# Revit family: ON5DRX-NRG
name_source: partatom
category: Mechanical Equipment
units: mm (PartAtom-declared; Revit-internal decimal feet)

## family parameters
Always vertical = Yes
Cut with Voids When Loaded = No
OmniClass Number = 23.40.40.11.17
OmniClass Title = Refrigerated Cases
Part Type = Normal
Room Calculation Point = No
Round Connector Dimension = Use Radius
Shared = No
Work Plane-Based = Yes

## types (8) — shared parameters
24" Shelf = Yes
BOTTOM ELECTRICAL = Yes
BOTTOM REFRIGERATION PIPING = Yes
Certifications = NSF 7, UL471, CSA
DATE = 03/21/2017
DRAIN PIPING = Yes
Default Elevation = 48"
Description = Rear Load Multi-Deck Merchandiser with Synerg-E™
Discharge Air Velocity (FPM) = 260 FPM
EQUIPMENT DESCRIPTION = Rear Load Multi-Deck Merchandiser with Synerg-E™
EQUIPMENT MARK = ON5DRX-NRG
GLASS = Glass
Height = 81 11/16"
High Efficiency Amps = 1 A
High Power (Cornice) Amps = 0 A
Item Description = Rear Load Multi-Deck Merchandiser with Synerg-E™
LF STD END = Yes
Legend Number = ON5DRX-NRG
Manufacturer = HILL PHOENIX
Model = ON5DRX-NRG
PAINTED METAL UPPER SHELF = PAINTED SHELVES
REAR REFRIGERATION PIPING = Yes
REFRIGERATION PIPING = COPPER PIPE
RT STD END = Yes
Refgn = 8 3/4"
STAINLESS STEEL = GALVANIZED STEEL
Standard Power Amps = 0 A
Superheat Set Point @ Bulb (°F) = 6 - 8 °F
TOP ELECTRICAL = Yes
TOP REFRIGERATION PIPING = Yes
Timed-Off Defrost Termination Temp = 42 °F
URL = http://www.hillphoenix.com
Width = 45 1/4"
zero-valued in all types: Defrosts Per Day, Number of Fans

## per-type parameters (varying)
| type | BTUH Conventional | BTUH Parallel | CENTER LINE | DRAIN LINE | Discharge Air (°F) | Door | Evaporator (°F) | High Efficiency Watts | High Power (Cornice) Watts | Length | Length of Cases | Light Length | Lights Per Row | Number of Doors | Standard Power Watts | Timed-Off Defrost Fail-Safe (Min) |
| 08' | 1478 | 1293 | 48" | 48" | 32 °F | Door_8 : 08'(Dairy,Deli,Cut Produce) | 28 °F | 50 W | 24 W | 96" | 96" | 3' | 2 | 2 | 9 W | 40 |
| 12' | 1435 | 1256 | 72" | 72" | 32 °F | Door_12 : 12'(Dairy,Deli,Cut Produce) | 28 °F | 100 W | 45 W | 144" | 144" | 4' | 3 | 3 | 18 W | 30 (Min) |
| Sample 1 (8') | 1404 | 1229 | 48" | 48" | 32 °F | Door_8 : 08'(Dairy,Deli,Cut Produce) | 28 °F | 50 W | 24 W | 96" | 96" | 3' | 2 | 2 | 9 W | 40 (Min) |
| Std. Dairy | 1380 | 1208 | 48" | 48" | 32 °F | Door_8 : 08'(Dairy,Deli,Cut Produce) | 28 °F | 67 W | 43 W | 96" | 96" | 4' | 2 | 2 | 24 W | 40 (Min) |
| 2.5" Ext | 1152 | 1120 | 48" | 48" | 37 °F | Door_8 : 08'(Dairy,Deli,Cut Produce) | 34 °F | 67 W | 43 W | 96" | 96" | 4' | 2 | 2 | 24 W | 40 (Min) |
| 5" Ext | 1101 | 1085 | 48" | 48" | 37 °F | Door_8 : 08'(Dairy,Deli,Cut Produce) | 34 °F | 67 W | 43 W | 96" | 96" | 4' | 2 | 2 | 24 W | 40 (Min) |
| 7.5" Ext | 1068 | 1053 | 48" | 48" | 37 °F | Door_8 : 08'(Dairy,Deli,Cut Produce) | 34 °F | 67 W | 43 W | 96" | 96" | 4' | 2 | 2 | 24 W | 40 (Min) |
| Sample 1 (6') 2 | 1404 | 1229 | 36" | 48" | 32 °F | Door_8 : 08'(Dairy,Deli,Cut Produce) | 28 °F | 50 W | 24 W | 72" | 96" | 3' | 2 | 2 | 9 W | 40 (Min) |

## geometry (parser evidence)
native form markers: Blend x16, Sweep x21
no freeform markers — native parametric forms only
